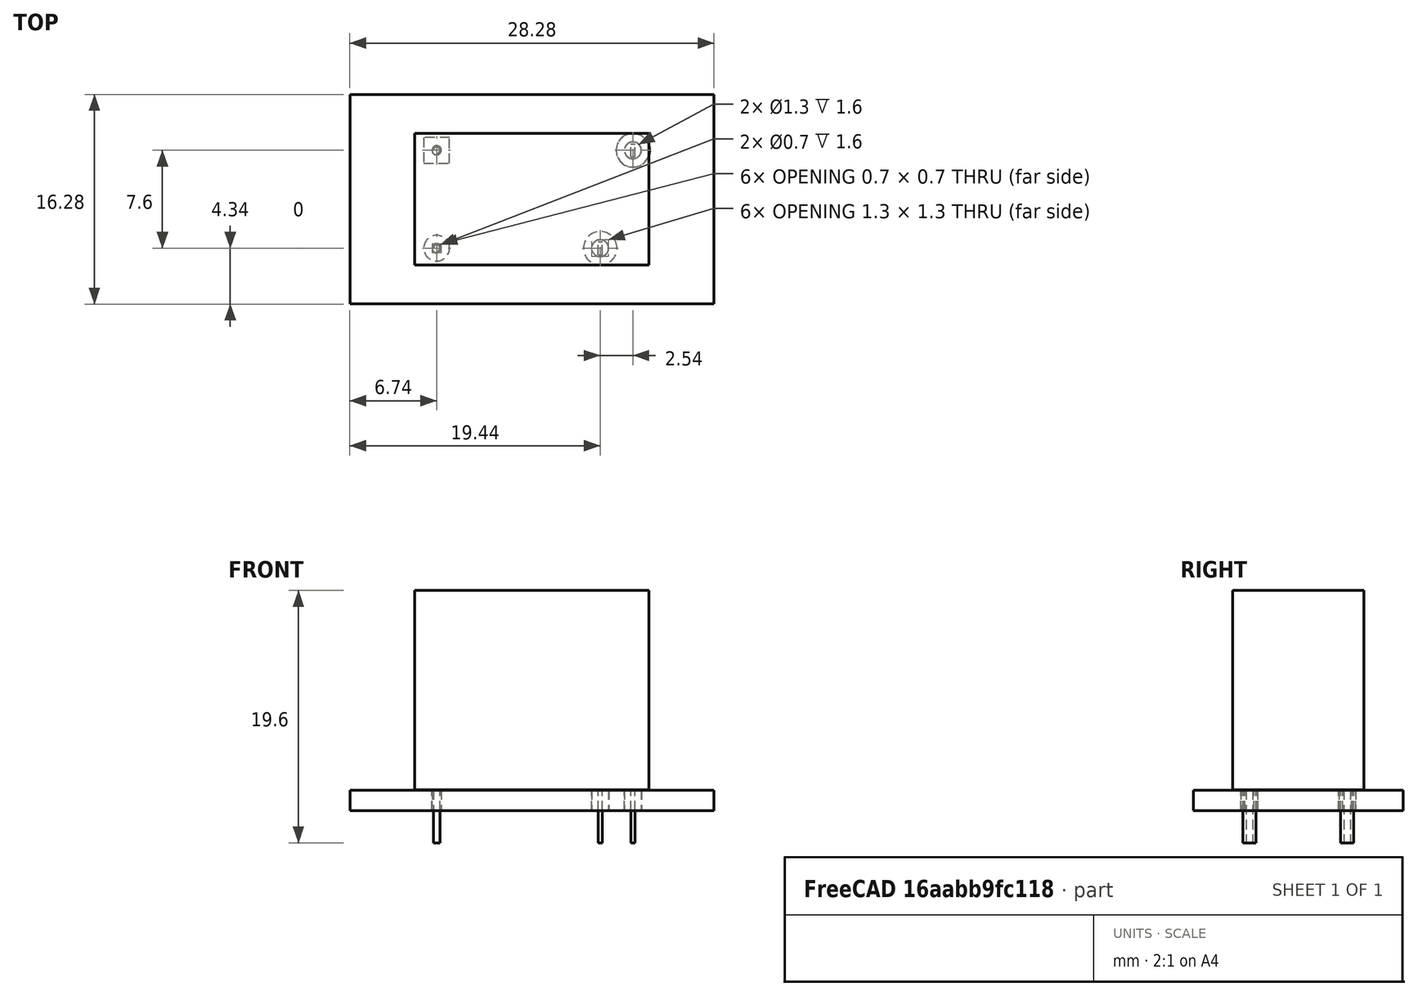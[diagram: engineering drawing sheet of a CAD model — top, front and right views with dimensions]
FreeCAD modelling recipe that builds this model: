
FCSTD DOCUMENT  (FreeCAD 0.21R33771 (Git))
Label: JY32FN
License: All rights reserved
LicenseURL: https://en.wikipedia.org/wiki/All_rights_reserved
objects: Part::Feature×10, Part::Box×3, Sketcher::SketchObject×3, Part::Cylinder×2, Part::MultiFuse×1, Part::Fuse×1, Part::Compound×1, App::DocumentObjectGroup×1
note: 21 computed .brp shape members not serialized (recipe doc carries the construction recipe); baked Part::Feature solids carry a one-line shape summary decoded from their .brp

FEATURE [Part::Box] cube
  AttacherType = Attacher::AttachEngine3D
  Height = 15.5
  Length = 18.2
  Placement = pos=(-1.7,-8.9,0) rot=(0,0,1;0rad)
  Width = 10.2
FEATURE [Part::Cylinder] cylinder
  Angle = 360
  AttacherType = Attacher::AttachEngine3D
  FirstAngle = 0
  Height = 4.1
  Placement = pos=(0,0,-4.1) rot=(0,0,1;0rad)
  Radius = 0.25
  SecondAngle = 0
FEATURE [Part::Cylinder] cylinder001
  Angle = 360
  AttacherType = Attacher::AttachEngine3D
  FirstAngle = 0
  Height = 4.1
  Placement = pos=(0,-7.6,-4.1) rot=(0,0,1;0rad)
  Radius = 0.25
  SecondAngle = 0
FEATURE [Part::Box] cube001
  AttacherType = Attacher::AttachEngine3D
  Height = 4.1
  Length = 0.3
  Placement = pos=(15.09,-0.5,-4.1) rot=(0,0,1;0rad)
  Width = 1
FEATURE [Part::Box] cube002
  AttacherType = Attacher::AttachEngine3D
  Height = 4.1
  Length = 0.3
  Placement = pos=(12.55,-8.1,-4.1) rot=(0,0,1;0rad)
  Width = 1
FEATURE [Part::MultiFuse] Group
  Shapes = -> [cylinder,cylinder001,cube001,cube002]
FEATURE [Part::Fuse] Group003  label="Relay_SPST_Jieying-JY32FNH-FormA"
  Base = -> cube
  Tool = -> Group
FEATURE [Part::Feature] anr_  label="drill_000"
  shape: bbox 1.32 x 1.32 x 1.6 mm, 4 faces (baked)
FEATURE [Part::Feature] anr_001  label="drill_001"
  shape: bbox 1.32 x 1.32 x 1.6 mm, 4 faces (baked)
FEATURE [Part::Feature] anr_002  label="drill_002"
  shape: bbox 0.7199 x 0.7199 x 1.6 mm, 4 faces (baked)
FEATURE [Part::Feature] anr_003  label="drill_003"
  shape: bbox 0.7199 x 0.7199 x 1.6 mm, 4 faces (baked)
FEATURE [Part::Compound] annulars  label="TH-Drills"
  Links = -> [anr_,anr_001,anr_002,anr_003]
FEATURE [Part::Feature] Shape001  label="topPads"
  Placement = pos=(0,0,-0.01) rot=(0,0,1;0rad)
  shape: bbox 17.54 x 10.2 x 0.01 mm, 23 faces, 4 solids (baked)
FEATURE [Part::Feature] Shape002  label="btmPads"
  Placement = pos=(0,0,-1.6) rot=(0,0,1;0rad)
  shape: bbox 17.54 x 10.2 x 0.01 mm, 23 faces, 4 solids (baked)
FEATURE [Part::Feature] Shape  label="F.SilkS_outline_"
  Placement = pos=(0,0,0.01) rot=(0,0,1;0rad)
  shape: bbox 18.52 x 10.52 x 2e-07 mm, 0 faces, 0 solids (baked)
FEATURE [Sketcher::SketchObject] _F_SilkS__sketch  label="F.SilkS_"
  FullyConstrained = false
  Placement = pos=(0,0,0.01) rot=(0,0,1;0rad)
  sketch-geometry (20):
    g0: LineSegment StartX=2.54 StartY=0 StartZ=0 EndX=3.81 EndY=0 EndZ=0
    g1: LineSegment StartX=2.54 StartY=-1.27 StartZ=0 EndX=3.81 EndY=-1.27 EndZ=0
    g2: LineSegment StartX=2.54 StartY=-2.54 StartZ=0 EndX=5.08 EndY=-3.81 EndZ=0
    g3: LineSegment StartX=2.54 StartY=-6.35 StartZ=0 EndX=2.54 EndY=-1.27 EndZ=0
    g4: LineSegment StartX=3.81 StartY=0 StartZ=0 EndX=3.81 EndY=-1.27 EndZ=0
    g5: LineSegment StartX=3.81 StartY=-1.27 StartZ=0 EndX=5.08 EndY=-1.27 EndZ=0
    g6: LineSegment StartX=3.81 StartY=-6.35 StartZ=0 EndX=3.81 EndY=-7.62 EndZ=0
    g7: LineSegment StartX=3.81 StartY=-7.62 StartZ=0 EndX=2.54 EndY=-7.62 EndZ=0
    g8: LineSegment StartX=5.08 StartY=-1.27 StartZ=0 EndX=5.08 EndY=-6.35 EndZ=0
    g9: LineSegment StartX=5.08 StartY=-6.35 StartZ=0 EndX=2.54 EndY=-6.35 EndZ=0
    g10: LineSegment StartX=12.6 StartY=0 StartZ=0 EndX=12.9 EndY=0.1 EndZ=0
    g11: LineSegment StartX=12.7 StartY=-1.8 StartZ=0 EndX=11.4 EndY=0.7 EndZ=0
    g12: LineSegment StartX=12.7 StartY=-5.8 StartZ=0 EndX=12.7 EndY=-1.8 EndZ=0
    g13: LineSegment StartX=12.9 StartY=0.1 StartZ=0 EndX=12.9 EndY=-0.1 EndZ=0
    g14: LineSegment StartX=12.9 StartY=-0.1 StartZ=0 EndX=12.6 EndY=0 EndZ=0
    g15: LineSegment StartX=13.6 StartY=0 StartZ=0 EndX=12.6 EndY=0 EndZ=0
    g16: LineSegment StartX=-1.8 StartY=1.4 StartZ=0 EndX=-1.8 EndY=-9 EndZ=0
    g17: LineSegment StartX=-1.8 StartY=-9 StartZ=0 EndX=16.6 EndY=-9 EndZ=0
    g18: LineSegment StartX=16.6 StartY=-9 StartZ=0 EndX=16.6 EndY=1.4 EndZ=0
    g19: LineSegment StartX=16.6 StartY=1.4 StartZ=0 EndX=-1.8 EndY=1.4 EndZ=0
  constraints (4):
    c: Coincident(g16,g17)
    c: Coincident(g17,g18)
    c: Coincident(g18,g19)
    c: Coincident(g19,g16)
FEATURE [Part::Feature] Shape003  label="F.CrtYd_outline_"
  Placement = pos=(0,0,0.01) rot=(0,0,1;0rad)
  shape: bbox 18.85 x 10.85 x 2e-07 mm, 0 faces, 0 solids (baked)
FEATURE [Sketcher::SketchObject] _F_CrtYd__sketch  label="F.CrtYd_"
  FullyConstrained = false
  Placement = pos=(0,0,0.01) rot=(0,0,1;0rad)
  sketch-geometry (4):
    g0: LineSegment StartX=-2 StartY=1.6 StartZ=0 EndX=-2 EndY=-9.2 EndZ=0
    g1: LineSegment StartX=-2 StartY=-9.2 StartZ=0 EndX=16.8 EndY=-9.2 EndZ=0
    g2: LineSegment StartX=16.8 StartY=-9.2 StartZ=0 EndX=16.8 EndY=1.6 EndZ=0
    g3: LineSegment StartX=16.8 StartY=1.6 StartZ=0 EndX=-2 EndY=1.6 EndZ=0
  constraints (4):
    c: Coincident(g0,g1)
    c: Coincident(g1,g2)
    c: Coincident(g2,g3)
    c: Coincident(g3,g0)
FEATURE [Part::Feature] Shape004  label="F.Fab_outline_"
  Placement = pos=(0,0,0.01) rot=(0,0,1;0rad)
  shape: bbox 18.32 x 10.32 x 2e-07 mm, 0 faces, 0 solids (baked)
FEATURE [Sketcher::SketchObject] _F_Fab__sketch  label="F.Fab_"
  FullyConstrained = false
  Placement = pos=(0,0,0.01) rot=(0,0,1;0rad)
  sketch-geometry (5):
    g0: LineSegment StartX=-1.7 StartY=-8.9 StartZ=0 EndX=-1.7 EndY=1.3 EndZ=0
    g1: LineSegment StartX=-1.7 StartY=-8.9 StartZ=0 EndX=16.5 EndY=-8.9 EndZ=0
    g2: LineSegment StartX=0 StartY=-1.8 StartZ=0 EndX=0 EndY=-5.8 EndZ=0
    g3: LineSegment StartX=16.5 StartY=1.3 StartZ=0 EndX=-1.7 EndY=1.3 EndZ=0
    g4: LineSegment StartX=16.5 StartY=-8.9 StartZ=0 EndX=16.5 EndY=1.3 EndZ=0
FEATURE [Part::Feature] PCB
  shape: bbox 28.28 x 16.28 x 1.58 mm, 14 faces (baked)
FEATURE [App::DocumentObjectGroup] Group004  label=""Relay_SPST_Jieying-JY32FNH-FormA"-fp"
  Group = -> [Shape001,Shape002,annulars,_F_SilkS__sketch,Shape,_F_CrtYd__sketch,Shape003,_F_Fab__sketch,Shape004,PCB]
